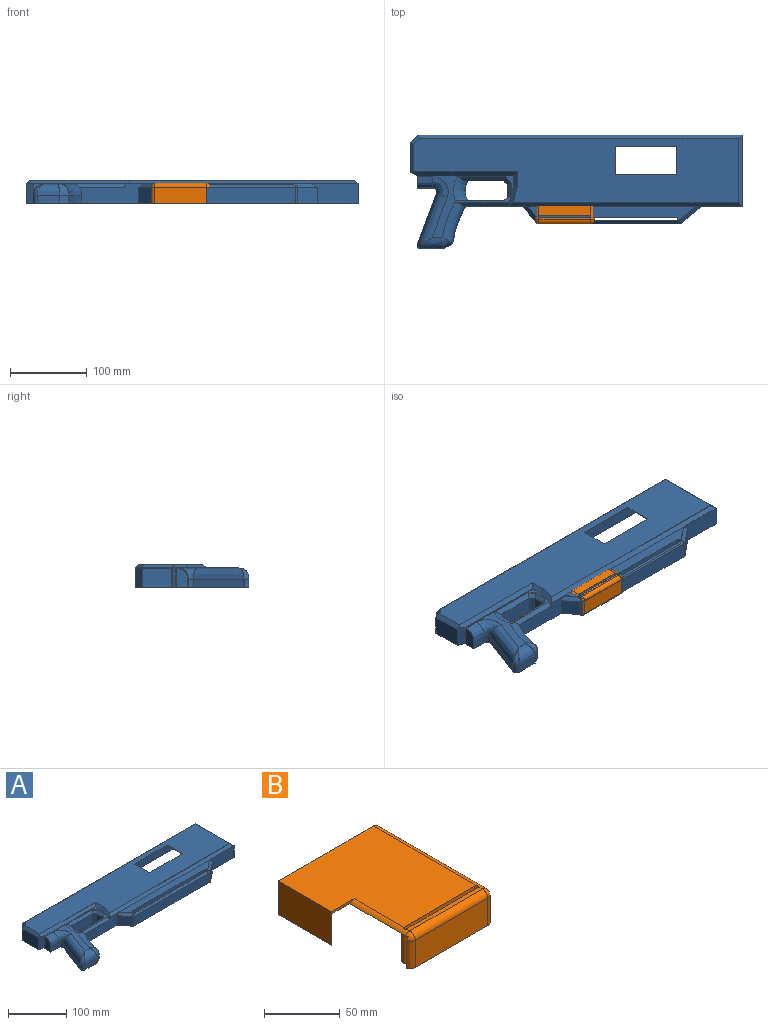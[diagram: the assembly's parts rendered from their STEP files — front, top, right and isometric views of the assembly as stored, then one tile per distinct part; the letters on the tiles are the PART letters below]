
ASSEMBLY  parts=2 mates=1
PART A: 132 faces, bbox 437.3x153.1x34.3 mm
  f0: plane 422.98x83.14mm, normal (0,0,1), area 26833.3mm2, adj f43,f44,f45,f46,f47,f48,f49,f50
  f1: plane 422.16x82.32mm, normal (0,0,-1), area 26414.1mm2, adj f104,f105,f106,f107,f108,f109,f110,f111
  f2: plane 93.14x25mm, normal (1,0,0), area 1571.7mm2, adj f3,f5,f36,f49,f127
  f3: plane 432.98x148.46mm, normal (0,0,-1), area 1380.7mm2, adj f2,f5,f6,f7,f8,f9,f10,f11
  f4: plane 180.31x6.76mm, normal (0,0,-1), area 365.2mm2, adj f55,f56,f57,f58,f116,f117,f118,f119
  f5: plane 60.18x25mm, normal (0,-1,0), area 1327.2mm2, adj f2,f3,f50,f59,f61
  f6: plane 19.73x10mm, normal (0,-1,0), area 197.3mm2, adj f3,f7,f21,f31
  f7: cylinder r=5mm len=10mm, axis (0,0,-1), area 96.5mm2, adj f3,f6,f8,f30
  f8: plane 65.62x24.71mm, normal (-0.94,0.35,0), area 701.1mm2, adj f3,f7,f9,f29
  f9: cylinder r=5mm len=10mm, axis (0,0,-1), area 96.5mm2, adj f3,f8,f10,f28
  f10: plane 29.47x10mm, normal (0,-1,0), area 294.7mm2, adj f3,f9,f11,f27
  f11: plane 11.59x10mm, normal (0.5,-0.86,0), area 134.2mm2, adj f3,f10,f12,f26
  f12: cylinder r=149.61mm len=48.55mm, axis (0,0,-1), area 516.7mm2, adj f3,f11,f13,f25
  f13: plane 85.43x25.72mm, normal (0,-1,0), area 1615.3mm2, adj f3,f12,f25,f32,f35,f50,f51,f65
  f14: plane 124.82x25mm, normal (0,1,0), area 3120.5mm2, adj f3,f21,f22,f33
  f15: plane 66.02x27.83mm, normal (0,1,0), area 1237.9mm2, adj f16,f20,f22,f23,f24
  f16: cylinder r=24.17mm len=26.09mm, axis (0,0,-1), area 275.6mm2, adj f15,f17,f23,f24
  f17: plane 55.82x22.91mm, normal (0,-1,0), area 954.4mm2, adj f16,f18,f23,f24,f40
  f18: plane 20x4.98mm, normal (-0.73,-0.69,0), area 136.9mm2, adj f17,f19,f23,f41
  f19: plane 20x17.29mm, normal (-1,0,0), area 345.9mm2, adj f18,f20,f23,f42
  f20: plane 25x9.69mm, normal (-0.63,0.78,0), area 167.2mm2, adj f15,f19,f22,f23,f42
  f21: plane 25x16.32mm, normal (-1,0,0), area 370.5mm2, adj f3,f6,f14,f22,f31
  f22: plane 124.84x80.48mm, normal (0,0,1), area 1368.9mm2, adj f14,f15,f20,f21,f24,f25,f26,f27
  f23: plane 57.12x28.09mm, normal (0,0,-1), area 154.3mm2, adj f15,f16,f17,f18,f19,f20,f76,f77
  f24: bspline ~42.28x18.82mm, area 634mm2, adj f15,f16,f17,f22,f40
  f25: bspline ~55.84x31.71mm, area 1181.4mm2, adj f12,f13,f22,f26,f32
  f26: bspline ~20.39x20.31mm, area 219.7mm2, adj f11,f22,f25,f27
  f27: bspline ~30.94x15mm, area 492.1mm2, adj f10,f22,f26,f28
  f28: bspline ~23.33x21.68mm, area 117.7mm2, adj f9,f27,f29
  f29: bspline ~70.9x38.75mm, area 1531.2mm2, adj f8,f22,f28,f30
  f30: bspline ~27.05x20.24mm, area 475.9mm2, adj f7,f22,f29,f31
  f31: bspline ~20.71x15mm, area 480.3mm2, adj f6,f21,f22,f30
  f32: plane 75.83x9.28mm, normal (0,-0.71,0.71), area 438.3mm2, adj f13,f22,f25,f35
  f33: plane 25x0.03mm, normal (-1,0,0), area 0.8mm2, adj f3,f14,f34,f44
  f34: plane 124.81x25mm, normal (0,-1,0), area 3120.2mm2, adj f3,f33,f39,f43
  f35: plane 5x5mm, normal (-0.97,0.24,0), area 12.9mm2, adj f13,f32,f45
  f36: plane 421.51x25mm, normal (0,1,0), area 10537.8mm2, adj f2,f3,f37,f48
  f37: plane 25x11.47mm, normal (-0.64,0.77,0), area 371.5mm2, adj f3,f36,f38,f47
  f38: plane 39.13x25mm, normal (-1,0,0), area 978.3mm2, adj f3,f37,f39,f46
  f39: plane 28.06x10.12mm, normal (-0.4,-0.92,0), area 292.6mm2, adj f3,f34,f38,f43,f46
  f40: plane 66.8x8.62mm, normal (0,-0.71,0.71), area 399.1mm2, adj f17,f22,f24,f41
  f41: plane 9.98x9.69mm, normal (-0.51,-0.48,0.71), area 63mm2, adj f18,f22,f40,f42
  f42: plane 19.28x5mm, normal (-0.71,0,0.71), area 114.9mm2, adj f19,f20,f22,f41
  f43: plane 136.87x5mm, normal (0,-0.71,0.71), area 932.2mm2, adj f0,f34,f39,f44,f46
  f44: plane 19.59x5mm, normal (-0.71,0,0.71), area 118.7mm2, adj f0,f22,f33,f43,f45
  f45: plane 26.21x11.55mm, normal (-0.69,0.17,0.71), area 170.5mm2, adj f0,f22,f35,f44,f50
  f46: plane 40.46x5mm, normal (-0.71,0,0.71), area 272.2mm2, adj f0,f38,f39,f43,f47
  f47: plane 13.26x11.81mm, normal (-0.45,0.55,0.71), area 90.4mm2, adj f0,f37,f46,f48
  f48: plane 421.51x5mm, normal (0,0.71,0.71), area 2956.5mm2, adj f0,f36,f47,f49
  f49: plane 93.14x5mm, normal (0.71,0,0.71), area 623.3mm2, adj f0,f2,f48,f50
  f50: plane 304.6x5mm, normal (0,-0.71,0.71), area 2113.6mm2, adj f0,f5,f13,f45,f49,f60
  f51: plane 20.75x20mm, normal (-0.77,-0.63,0), area 537.1mm2, adj f3,f13,f52,f65
  f52: cylinder r=5mm len=20mm, axis (0,0,-1), area 88.3mm2, adj f3,f51,f53,f64
  f53: plane 183.24x20mm, normal (0,-1,0), area 3664.8mm2, adj f3,f52,f54,f63
  f54: cylinder r=5mm len=20mm, axis (0,0,-1), area 68.7mm2, adj f3,f53,f59,f62
  f55: plane 173.55x25mm, normal (0,-1,0), area 4338.8mm2, adj f4,f56,f58,f60
  f56: cylinder r=2.38mm len=25mm, axis (0,0,-1), area 185.5mm2, adj f4,f55,f57,f60,f63
  f57: plane 173.55x23.75mm, normal (0,1,0), area 4121.8mm2, adj f4,f56,f58,f63
  f58: cylinder r=2.38mm len=25mm, axis (0,0,-1), area 185.5mm2, adj f4,f55,f57,f60,f63
  f59: plane 26.12x21.45mm, normal (0.63,-0.77,0), area 676mm2, adj f3,f5,f54,f61
  f60: plane 219.09x17.58mm, normal (0,0,1), area 2913mm2, adj f50,f55,f56,f58,f61,f63,f65
  f61: plane 29.3x21.45mm, normal (0.45,-0.55,0.71), area 217.5mm2, adj f5,f59,f60,f62
  f62: cone r=5mm half-angle=45deg, axis (0,0,-1), area 12.2mm2, adj f54,f61,f63
  f63: plane 187.07x8.83mm, normal (0,-0.71,0.71), area 983.6mm2, adj f53,f56,f57,f58,f60,f62,f64
  f64: cone r=5mm half-angle=45deg, axis (0,0,-1), area 24.9mm2, adj f52,f63,f65
  f65: plane 20.9x20.75mm, normal (-0.55,-0.45,0.71), area 175.4mm2, adj f13,f51,f60,f64
  f66: plane 59.54x24.59mm, normal (0,1,0), area 1289.7mm2, adj f3,f96,f111,f120,f122
  f67: plane 18.73x10mm, normal (0,1,0), area 187.3mm2, adj f3,f68,f82,f91
  f68: cylinder r=6mm len=10mm, axis (0,0,-1), area 115.9mm2, adj f3,f67,f69,f90
  f69: plane 65.62x24.71mm, normal (0.94,-0.35,0), area 701.1mm2, adj f3,f68,f70,f89
  f70: cylinder r=4mm len=10mm, axis (0,0,-1), area 77.2mm2, adj f3,f69,f71,f88
  f71: plane 29.2x10mm, normal (0,1,0), area 292mm2, adj f3,f70,f72,f87
  f72: plane 10.95x10mm, normal (-0.5,0.86,0), area 126.8mm2, adj f3,f71,f73,f86
  f73: cylinder r=150.61mm len=48.92mm, axis (0,0,-1), area 521.3mm2, adj f3,f72,f74,f85
  f74: plane 86.59x25.85mm, normal (0,1,0), area 1600.4mm2, adj f3,f73,f85,f92,f95,f111,f112,f126
  f75: plane 124.82x24.59mm, normal (0,-1,0), area 2995.9mm2, adj f3,f82,f83,f93,f105
  f76: plane 66.28x27.1mm, normal (0,-1,0), area 1204.9mm2, adj f23,f77,f81,f83,f84
  f77: cylinder r=25.17mm len=28.09mm, axis (0,0,-1), area 298mm2, adj f23,f76,f78,f84
  f78: plane 57.11x22.72mm, normal (0,1,0), area 953.8mm2, adj f23,f77,f79,f84,f101
  f79: plane 19.59x5.59mm, normal (0.73,0.69,0), area 150.3mm2, adj f23,f78,f80,f102
  f80: plane 19.59x18.17mm, normal (1,0,0), area 355.8mm2, adj f23,f79,f81,f103
  f81: plane 24x9.75mm, normal (0.63,-0.78,0), area 177.5mm2, adj f23,f76,f80,f83,f103
  f82: plane 25.34x15.66mm, normal (1,0,0), area 311.6mm2, adj f3,f67,f75,f83,f91
  f83: plane 124.27x79.49mm, normal (0,0,-1), area 1115.2mm2, adj f75,f76,f81,f82,f84,f85,f86,f87
  f84: offset ~45.71x21.1mm, area 631.8mm2, adj f76,f77,f78,f83,f101
  f85: offset ~57.94x33.91mm, area 1117.8mm2, adj f73,f74,f83,f86,f92
  f86: offset ~22.39x22.31mm, area 195.7mm2, adj f72,f83,f85,f87
  f87: offset ~32.94x17mm, area 457.3mm2, adj f71,f83,f86,f88
  f88: bspline ~20.23x16.6mm, area 88mm2, adj f70,f87,f89
  f89: offset ~72.9x40.75mm, area 1432.4mm2, adj f69,f83,f88,f90
  f90: offset ~29.05x22mm, area 473.2mm2, adj f68,f83,f89,f91
  f91: offset ~22.71x17mm, area 426.6mm2, adj f67,f82,f83,f90
  f92: plane 76.53x8.93mm, normal (0,0.71,-0.71), area 397.2mm2, adj f74,f83,f85,f95,f106
  f93: plane 24.59x2.03mm, normal (1,0,0), area 50mm2, adj f3,f75,f94,f105
  f94: plane 125.6x24.59mm, normal (0,1,0), area 3088mm2, adj f3,f93,f100,f104
  f95: plane 5x5mm, normal (0.97,-0.24,0), area 12.9mm2, adj f74,f92,f106
  f96: plane 91.14x24.59mm, normal (-1,0,0), area 1484mm2, adj f3,f66,f97,f110,f127
  f97: plane 420.16x24.59mm, normal (0,-1,0), area 10329.8mm2, adj f3,f96,f98,f109
  f98: plane 24.59x10.83mm, normal (0.64,-0.77,0), area 344.9mm2, adj f3,f97,f99,f108
  f99: plane 38.01x24.59mm, normal (1,0,0), area 934.4mm2, adj f3,f98,f100,f107
  f100: plane 27.41x9.33mm, normal (0.4,0.92,0), area 264.3mm2, adj f3,f94,f99,f104,f107
  f101: plane 66.52x7.78mm, normal (0,0.71,-0.71), area 356.7mm2, adj f78,f83,f84,f102
  f102: plane 10x9.67mm, normal (0.51,0.48,-0.71), area 59.3mm2, adj f79,f83,f101,f103
  f103: plane 19.92x4.41mm, normal (0.71,0,-0.71), area 107.7mm2, adj f80,f81,f83,f102
  f104: plane 136.52x4.41mm, normal (0,0.71,-0.71), area 823.7mm2, adj f1,f94,f100,f105,f107
  f105: plane 20.05x5mm, normal (0.71,0,-0.71), area 120.5mm2, adj f1,f75,f83,f93,f104,f106
  f106: plane 25.16x10.68mm, normal (0.69,-0.17,-0.71), area 162.9mm2, adj f1,f83,f92,f95,f105,f111
  f107: plane 39.23x4.41mm, normal (0.71,0,-0.71), area 234.1mm2, adj f1,f99,f100,f104,f108
  f108: plane 12.41x11mm, normal (0.45,-0.55,-0.71), area 76.1mm2, adj f1,f98,f107,f109
  f109: plane 420.16x4.41mm, normal (0,-0.71,-0.71), area 2604.2mm2, adj f1,f97,f108,f110
  f110: plane 91.14x4.41mm, normal (-0.71,0,-0.71), area 541.4mm2, adj f1,f96,f109,f111
  f111: plane 302.32x5mm, normal (0,0.71,-0.71), area 2036.9mm2, adj f1,f66,f74,f106,f110,f121,f122,f126
  f112: plane 21.12x19.59mm, normal (0.77,0.63,0), area 535.2mm2, adj f3,f74,f113,f126
  f113: cylinder r=4mm len=19.59mm, axis (0,0,-1), area 69.2mm2, adj f3,f112,f114,f125
  f114: plane 183.24x19.59mm, normal (0,1,0), area 3588.9mm2, adj f3,f113,f115,f124
  f115: cylinder r=4mm len=19.59mm, axis (0,0,-1), area 53.9mm2, adj f3,f114,f120,f123
  f116: plane 173.55x24mm, normal (0,1,0), area 4165.2mm2, adj f4,f117,f119,f121
  f117: cylinder r=3.38mm len=24mm, axis (0,0,-1), area 248.9mm2, adj f4,f116,f118,f121,f124
  f118: plane 173.55x21.34mm, normal (0,-1,0), area 3702.8mm2, adj f4,f117,f119,f124
  f119: cylinder r=3.38mm len=24mm, axis (0,0,-1), area 248.9mm2, adj f4,f116,f118,f121,f124
  f120: plane 26.4x21.67mm, normal (-0.63,0.77,0), area 669mm2, adj f3,f66,f115,f122
  f121: plane 218.75x17.58mm, normal (0,0,-1), area 2796.5mm2, adj f111,f116,f117,f119,f122,f124,f126
  f122: plane 29.09x21.67mm, normal (-0.45,0.55,-0.71), area 196.8mm2, adj f66,f111,f120,f121,f123,f124
  f123: cone r=4.29mm half-angle=45deg, axis (0,0,-1), area 7.8mm2, adj f115,f122,f124
  f124: plane 184.42x5.59mm, normal (0,0.71,-0.71), area 471.3mm2, adj f114,f117,f118,f119,f121,f122,f123,f125
  f125: cone r=4.29mm half-angle=45deg, axis (0,0,-1), area 10mm2, adj f113,f124,f126
  f126: plane 21.12x20.63mm, normal (0.55,0.45,-0.71), area 159.5mm2, adj f74,f111,f112,f121,f124,f125
  f127: cylinder r=21.95mm len=43.9mm, axis (1,0,0), area 69mm2, adj f2,f3,f96
  f128: plane 79.97x1mm, normal (0,-1,0), area 80mm2, adj f0,f1,f129,f131
  f129: plane 36.75x1mm, normal (1,0,0), area 36.8mm2, adj f0,f1,f128,f130
  f130: plane 79.97x1mm, normal (0,1,0), area 80mm2, adj f0,f1,f129,f131
  f131: plane 36.75x1mm, normal (-1,0,0), area 36.8mm2, adj f0,f1,f128,f130
PART B: 45 faces, bbox 93.7x106.5x27 mm
  f0: plane 77.19x13.52mm, normal (0,0,-1), area 88.2mm2, adj f1,f5,f12,f13,f14,f27,f28,f29
  f1: plane 22x8.52mm, normal (1,0,0), area 187.5mm2, adj f0,f4,f14,f40
  f2: plane 92.69x27mm, normal (0,1,0), area 192mm2, adj f4,f7,f8,f15,f39,f44
  f3: plane 27x21.11mm, normal (0,-1,0), area 45.6mm2, adj f7,f8,f15,f22,f39,f44
  f4: cylinder r=5mm len=101.53mm, axis (0,-1,0), area 498mm2, adj f1,f2,f8,f16,f17,f19,f40,f44
  f5: plane 22x8.52mm, normal (-1,0,0), area 187.5mm2, adj f0,f6,f29,f40
  f6: cylinder r=4mm len=100.53mm, axis (0,-1,0), area 316mm2, adj f5,f23,f30,f33,f34,f35,f40,f44
  f7: plane 49.65x0.36mm, normal (0,0,-1), area 17.9mm2, adj f2,f3,f15,f39
  f8: plane 96.4x88.69mm, normal (0,0,1), area 7518.7mm2, adj f2,f3,f4,f10,f11,f15,f16,f22
  f9: plane 66.02x27mm, normal (0,1,0), area 1782.5mm2, adj f10,f16,f17,f18
  f10: cylinder r=1.36mm len=27mm, axis (0,0,-1), area 115mm2, adj f8,f9,f11,f17,f18,f22
  f11: plane 66.02x27mm, normal (0,-1,0), area 1782.5mm2, adj f8,f10,f16,f18
  f12: cylinder r=5mm len=22mm, axis (0,0,-1), area 129mm2, adj f0,f13,f21,f41
  f13: plane 67.58x22mm, normal (0,-1,0), area 1486.8mm2, adj f0,f12,f14,f20
  f14: cylinder r=5mm len=22mm, axis (0,0,-1), area 172.8mm2, adj f0,f1,f13,f19
  f15: plane 49.65x27mm, normal (-1,0,0), area 1340.4mm2, adj f2,f3,f7,f8
  f16: cylinder r=1.36mm len=27mm, axis (0,0,-1), area 115.2mm2, adj f4,f8,f9,f11,f17,f18
  f17: plane 67.58x3.72mm, normal (0,0,1), area 207.6mm2, adj f4,f9,f10,f16,f20,f22
  f18: plane 70.73x4.72mm, normal (0,0,-1), area 143.7mm2, adj f9,f10,f11,f16,f24,f25,f26,f33
  f19: sphere r=5mm, area 39.3mm2, adj f4,f14,f20
  f20: cylinder r=5mm len=67.58mm, axis (-1,0,0), area 530.8mm2, adj f13,f17,f19,f21
  f21: sphere r=5mm, area 32.8mm2, adj f12,f20,f22,f41,f44
  f22: cylinder r=5mm len=51.89mm, axis (0,1,0), area 238.8mm2, adj f3,f8,f10,f17,f21,f44
  f23: plane 94.05x87.69mm, normal (0,0,-1), area 7293.6mm2, adj f6,f25,f26,f30,f31,f32,f33,f38
  f24: plane 66.02x26mm, normal (0,-1,0), area 1716.4mm2, adj f18,f25,f33,f34
  f25: cylinder r=2.36mm len=26mm, axis (0,0,-1), area 190.9mm2, adj f18,f23,f24,f26,f34,f38
  f26: plane 66.02x26mm, normal (0,1,0), area 1716.4mm2, adj f18,f23,f25,f33
  f27: cylinder r=4mm len=22mm, axis (0,0,-1), area 93.7mm2, adj f0,f28,f37,f41
  f28: plane 67.58x22mm, normal (0,1,0), area 1486.8mm2, adj f0,f27,f29,f36
  f29: cylinder r=4mm len=22mm, axis (0,0,-1), area 138.2mm2, adj f0,f5,f28,f35
  f30: plane 90.33x1mm, normal (0,-1,0), area 89.5mm2, adj f6,f23,f31,f44
  f31: plane 47.65x1mm, normal (1,0,0), area 47.6mm2, adj f23,f30,f32,f44
  f32: plane 20.11x1mm, normal (0,1,0), area 18.3mm2, adj f23,f31,f38,f44
  f33: cylinder r=2.36mm len=26mm, axis (0,0,-1), area 192.1mm2, adj f6,f18,f23,f24,f26,f34
  f34: plane 67.58x2.37mm, normal (0,0,-1), area 139.9mm2, adj f6,f24,f25,f33,f36,f38
  f35: sphere r=4mm, area 25.1mm2, adj f6,f29,f36
  f36: cylinder r=4mm len=67.58mm, axis (-1,0,0), area 424.6mm2, adj f28,f34,f35,f37
  f37: sphere r=4mm, area 18.2mm2, adj f27,f36,f38,f41,f44
  f38: cylinder r=4mm len=52.89mm, axis (0,1,0), area 145.9mm2, adj f23,f25,f32,f34,f37,f42,f43,f44
  f39: plane 49.65x25mm, normal (1,0,0), area 1241.1mm2, adj f2,f3,f7,f44
  f40: plane 25x2.35mm, normal (0,1,0), area 25.3mm2, adj f0,f1,f4,f5,f6,f44
  f41: plane 25x2.81mm, normal (0,1,0), area 28.2mm2, adj f0,f12,f21,f27,f37,f44
  f42: plane 0.2x0.02mm, normal (-0.99,0.12,0), area 0mm2, adj f38,f43,f44
  f43: plane 0.07x0.02mm, normal (-0.94,-0.33,0), area 0mm2, adj f38,f42,f44
  f44: plane 103.47x92.33mm, normal (0,0,-1), area 338.6mm2, adj f2,f3,f4,f6,f21,f22,f30,f31
PLACE A at identity
PLACE B t=(-108.71,3.4,-1)mm
MATE planar B.f13 <-> A.f53  axis (0,-1,0) through (33.22,-22.58,10)mm
